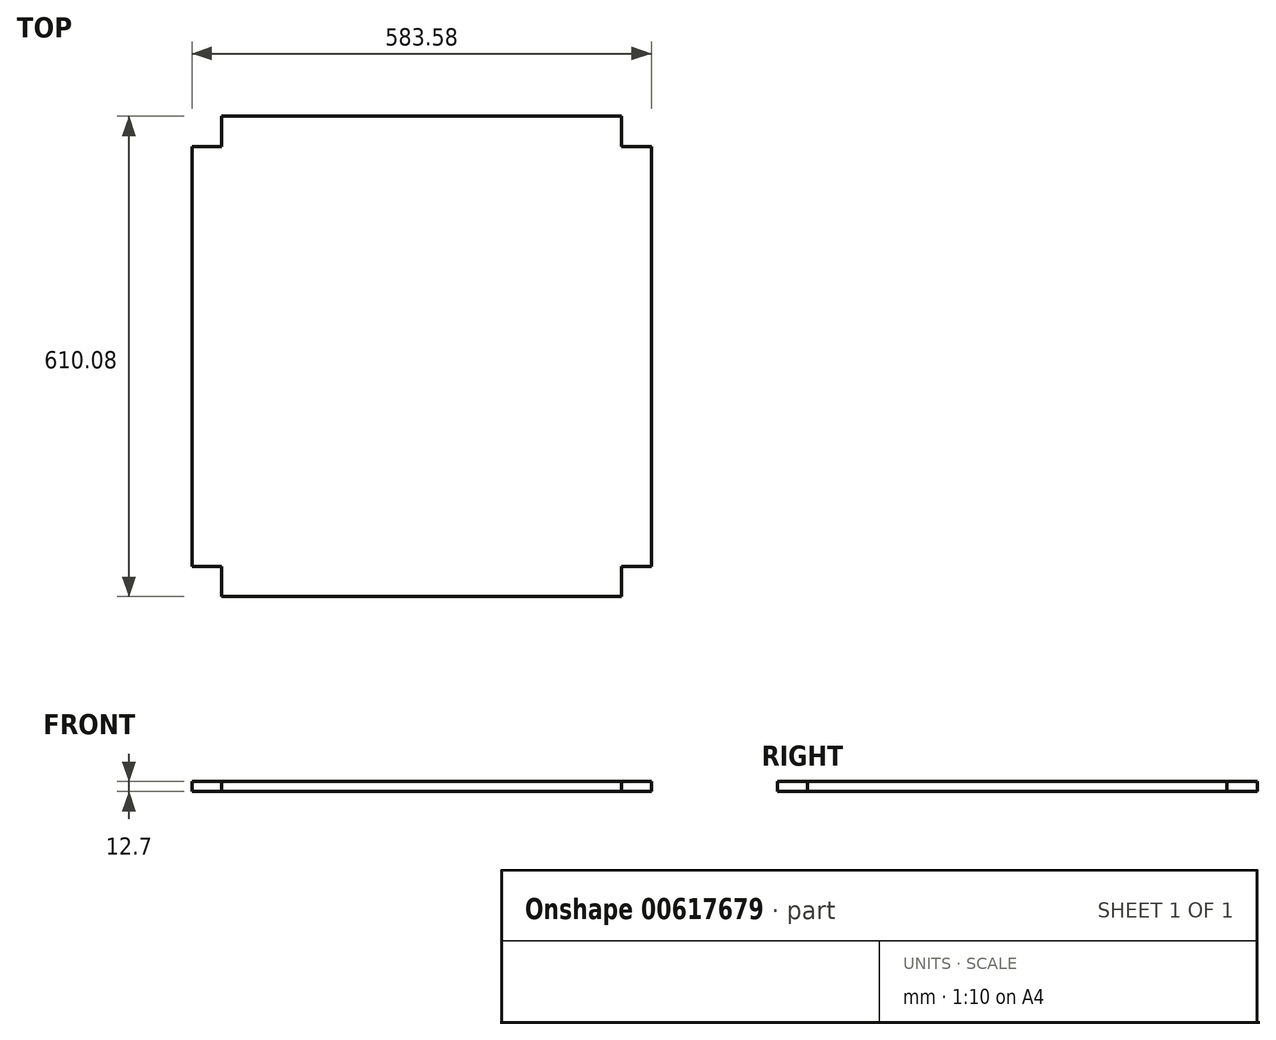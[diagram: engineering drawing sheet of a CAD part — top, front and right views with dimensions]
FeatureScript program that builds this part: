
annotation { "Feature Type Name" : "Feature", "Feature Type Description" : "" }
export const myFeature = defineFeature(function(context is Context, id is Id, definition is map)
    precondition{}
    {
        {
            var Q0;
            Q0=qCreatedBy(makeId("Top.planeOp"),FACE);
            var sketch = newSketch(context, id + "F0", { "sketchPlane" : qUnion([Q0])});
            skLineSegment(sketch, "E0.bottom", {"start": v(-50.12, -50.8) * mm, "end": v(533.46, -50.8) * mm});
            skLineSegment(sketch, "E0.top", {"start": v(-50.12, 559.28) * mm, "end": v(533.46, 559.28) * mm});
            skLineSegment(sketch, "E0.left", {"start": v(-50.12, -50.8) * mm, "end": v(-50.12, 559.28) * mm});
            skLineSegment(sketch, "E0.right", {"start": v(533.46, -50.8) * mm, "end": v(533.46, 559.28) * mm});
            skLineSegment(sketch, "E1.bottom", {"start": v(-50.12, -50.8) * mm, "end": v(0, -50.8) * mm});
            skLineSegment(sketch, "E1.left", {"start": v(-50.12, -50.8) * mm, "end": v(-50.12, 0) * mm});
            skLineSegment(sketch, "E2.bottom", {"start": v(533.46, -50.8) * mm, "end": v(495.42, -50.8) * mm});
            skLineSegment(sketch, "E2.top", {"start": v(533.46, -12.37) * mm, "end": v(495.42, -12.37) * mm});
            skLineSegment(sketch, "E2.left", {"start": v(533.46, -50.8) * mm, "end": v(533.46, -12.37) * mm});
            skLineSegment(sketch, "E2.right", {"start": v(495.42, -50.8) * mm, "end": v(495.42, -12.37) * mm});
            skLineSegment(sketch, "E3.bottom", {"start": v(-50.12, 559.28) * mm, "end": v(0, 559.28) * mm});
            skLineSegment(sketch, "E3.left", {"start": v(-50.12, 559.28) * mm, "end": v(-50.12, 508.48) * mm});
            skLineSegment(sketch, "E4.bottom", {"start": v(533.46, 559.28) * mm, "end": v(495.75, 559.28) * mm});
            skLineSegment(sketch, "E4.top", {"start": v(533.46, 520.62) * mm, "end": v(495.75, 520.62) * mm});
            skLineSegment(sketch, "E4.left", {"start": v(533.46, 559.28) * mm, "end": v(533.46, 520.62) * mm});
            skLineSegment(sketch, "E4.right", {"start": v(495.75, 559.28) * mm, "end": v(495.75, 520.62) * mm});
            skLineSegment(sketch, "E5.bottom", {"start": v(-50.12, -50.8) * mm, "end": v(-12.53, -50.8) * mm});
            skLineSegment(sketch, "E5.top", {"start": v(-50.12, -12.38) * mm, "end": v(-12.53, -12.38) * mm});
            skLineSegment(sketch, "E5.left", {"start": v(-50.12, -50.8) * mm, "end": v(-50.12, -12.38) * mm});
            skLineSegment(sketch, "E5.right", {"start": v(-12.53, -50.8) * mm, "end": v(-12.53, -12.38) * mm});
            skLineSegment(sketch, "E6.bottom", {"start": v(-50.12, 559.28) * mm, "end": v(-12.71, 559.28) * mm});
            skLineSegment(sketch, "E6.top", {"start": v(-50.12, 520.91) * mm, "end": v(-12.71, 520.91) * mm});
            skLineSegment(sketch, "E6.left", {"start": v(-50.12, 559.28) * mm, "end": v(-50.12, 520.91) * mm});
            skLineSegment(sketch, "E6.right", {"start": v(-12.71, 559.28) * mm, "end": v(-12.71, 520.91) * mm});
            skSolve(sketch);
        }
        {
            var Q0;
            Q0=makeQuery(id+"F0.imprint","IMPRINT",FACE,{"disambiguationData":[TD([[makeQuery(id+"F0.imprint","IMPRINT",EDGE,{"derivedFrom":sQuery(id+"F0.wireOp",EDGE,"E0.bottom")}),1.0]])]});
            extrude(context, id + "F1", {"entities" : qUnion([Q0]), "endBound" : BoundingType.SYMMETRIC, "depth" : 12.7 * mm, "offsetDistance" : 25.4 * mm});
        }
    });
